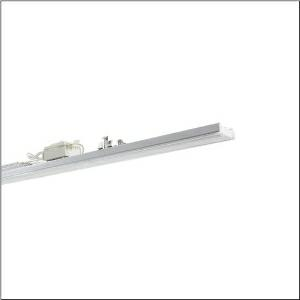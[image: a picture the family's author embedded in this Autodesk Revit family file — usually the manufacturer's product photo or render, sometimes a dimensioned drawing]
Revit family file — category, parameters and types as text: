
# Revit family: licross_11_recessed_mo_51tl11cn49xg
name_source: partatom
category: Lighting Fixtures
units: mm (PartAtom-declared; Revit-internal decimal feet)

## family parameters
Cut with Voids When Loaded = No
Host = Face
Light Source = No
Part Type = Normal
Room Calculation Point = No
Round Connector Dimension = Use Diameter
Shared = No

## types (1)
- --- (1 x LED, 9160 lm, 49.3 W, 4000K)
    Apparent Load = 49 VA
    CIE Flux Codes = 89 96 99 100 100
    Color Rendering = 80
    Color Temperature = 4000K
    Default Elevation = 1800 mm
    Description = Licross 11 Recessed MO, luminaire insert, of sheet steel, coil coated, white, length: 1.500mm, width: 66mm, height: 67mm, LED rated luminous flux: 9.160lm, light colour: 840, SDCM (Standard Deviation of Colour Matching)MacAdam ≤ 2 SDCM (initial), control gear: ON/OFF Multilumen, CLOi, with plug, 3-pole, with phase selection, mains connection: 220..240V, AC, 50/60Hz, start of lifetime: 49W, end of service life: 55W, internal wiring halogen-free, primary light control with lens, of plastic, primary optical cover: cover, of PMMA, light emission: direct distribution, primary light characteristic: symmetric, protection rating (complete): IP40, insulation class (complete): insulation class I (protective earthing), certification: CE, ENEC, VDE, UKCA, protection symbol: D if used in an environment without relevant dust loads with corresponding accessories, impact resistance: IK06, permissible ambient temperature for indoor applications: -35..+40°C, corresponds to IFS (International Featured Standards) requirements for safety and quality in the food industry, reducing of maximum allowable ambient temperature of 5°C with ceiling mounting, LABS conformity tested according to VDMA 24364:2018-05, The light source and the operating device comply with the requirements of the Ecodesign Regulation (EU) 2019/2020 and are replaceable in accordance with this regulation, packaging unit: 1 piece
    Height = 58 mm
    Lamp = 1 x LED
    Lamp Light Flux = 9160 lm
    Lamp Power = 49.3 W
    Lamp count = 1
    Length = 1500 mm
    Luminous efficacy = 186 lm/W
    Manufacturer = Siteco
    ModVariant = No
    Model = 51TL11CN49XG
    Mounting Place = Ceiling
    Mounting Type = Pendant
    Number of Poles = 1
    OnlyDefault = Yes
    Power Factor = 1
    Product Name = Licross 11 Recessed MO
    Product group = luminaire insert | ceiling pendant
    ProductGroupID = 901
    Protection Class = Protection class I
    Protection Degree = IP 40
    RLX_Detail_Level = 1
    RLX_Emergency_Light_Flux = 0 lm
    RLX_Emergency_Type = 0
    RLX_Emergency_Type_DB = No
    RlxData = <blob elided: 22541 chars, md5=4a2fc838>
    Socket = socket
    Standby Power = 0 W
    System Light Flux = 9160 lm
    System Power = 49 W
    Type Comments = factory setting: luminous flux: 100 % | (A | C | E) | 113 mA
    Type Image = l_1296930.jpg
    URL = http://relux.com
    VarID = @adj_089811
    Voltage = 0 V
    Weight = 0.00 kg
    Width = 66 mm

## geometry (parser evidence)
native form markers: Blend x4, Sweep x9
no freeform markers — native parametric forms only
